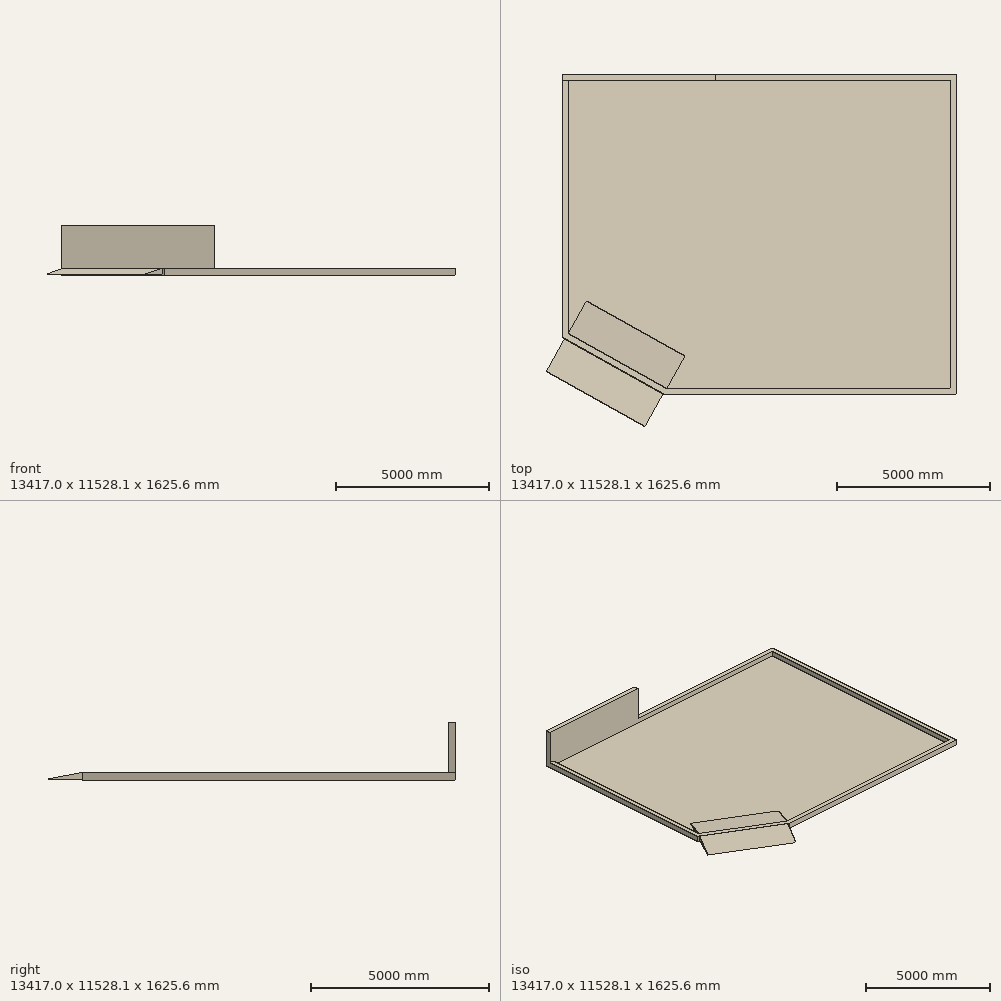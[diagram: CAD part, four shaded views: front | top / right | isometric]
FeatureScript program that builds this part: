
annotation { "Feature Type Name" : "Feature", "Feature Type Description" : "" }
export const myFeature = defineFeature(function(context is Context, id is Id, definition is map)
    precondition{}
    {
        {
            var Q0;
            Q0=qCreatedBy(makeId("Top.planeOp"),FACE);
            var sketch = newSketch(context, id + "F0", { "sketchPlane" : qUnion([Q0])});
            skLineSegment(sketch, "E0", {"start": v(-3030.3, -3459.43) * mm, "end": v(6240.7, -3459.43) * mm});
            skLineSegment(sketch, "E1", {"start": v(6240.7, -3459.43) * mm, "end": v(6240.7, 6624.37) * mm});
            skLineSegment(sketch, "E2", {"start": v(6240.7, 6624.37) * mm, "end": v(-6256.1, 6624.37) * mm});
            skLineSegment(sketch, "E3", {"start": v(-6256.1, 6624.37) * mm, "end": v(-6256.1, -1656.03) * mm});
            skLineSegment(sketch, "E4", {"start": v(-6256.1, -1656.03) * mm, "end": v(-3030.3, -3459.43) * mm});
            skLineSegment(sketch, "E5.0", {"start": v(6443.9, 6827.57) * mm, "end": v(-6459.3, 6827.57) * mm});
            skLineSegment(sketch, "E6.0", {"start": v(6443.9, -3662.63) * mm, "end": v(6443.9, 6827.57) * mm});
            skLineSegment(sketch, "E7.0", {"start": v(-3083.25, -3662.63) * mm, "end": v(6443.9, -3662.63) * mm});
            skLineSegment(sketch, "E8.0", {"start": v(-6459.3, 6827.57) * mm, "end": v(-6459.3, -1775.23) * mm});
            skLineSegment(sketch, "E9.0", {"start": v(-6459.3, -1775.23) * mm, "end": v(-3083.25, -3662.63) * mm});
            skLineSegment(sketch, "E10.filletArc", {"start": v(-6459.3, 6827.57) * mm, "end": v(-6459.3, 6827.57) * mm});
            skLineSegment(sketch, "E11.filletArc", {"start": v(6443.9, 6827.57) * mm, "end": v(6443.9, 6827.57) * mm});
            skLineSegment(sketch, "E12.filletArc", {"start": v(6443.9, -3662.63) * mm, "end": v(6443.9, -3662.63) * mm});
            skLineSegment(sketch, "E13.filletArc", {"start": v(-3083.25, -3662.63) * mm, "end": v(-3083.25, -3662.63) * mm});
            skLineSegment(sketch, "E14.filletArc", {"start": v(-6459.3, -1775.23) * mm, "end": v(-6459.3, -1775.23) * mm});
            skSolve(sketch);
        }
        {
            var Q0;
            Q0=makeQuery(id+"F0.imprint","IMPRINT",FACE,{"disambiguationData":[TD([[makeQuery(id+"F0.imprint","IMPRINT",EDGE,{"derivedFrom":sQuery(id+"F0.wireOp",EDGE,"E0")}),-1.0]])]});
            extrude(context, id + "F1", {"entities" : qUnion([Q0]), "depth" : 203.2 * mm, "offsetDistance" : 25.4 * mm});
        }
        {
            var Q0;
            Q0=makeQuery(id+"F1.opExtrude","CAP_FACE",FACE,{"disambiguationData":[OSD([sQuery(id+"F0.wireOp",EDGE,"E0"),sQuery(id+"F0.wireOp",EDGE,"E1"),sQuery(id+"F0.wireOp",EDGE,"E2"),sQuery(id+"F0.wireOp",EDGE,"E3"),sQuery(id+"F0.wireOp",EDGE,"E4"),sQuery(id+"F0.wireOp",EDGE,"E5.0"),sQuery(id+"F0.wireOp",EDGE,"E6.0"),sQuery(id+"F0.wireOp",EDGE,"E7.0"),sQuery(id+"F0.wireOp",EDGE,"E8.0"),sQuery(id+"F0.wireOp",EDGE,"E9.0")])],"isStart":false});
            var sketch = newSketch(context, id + "F2", { "sketchPlane" : qUnion([Q0])});
            skLineSegment(sketch, "E15.bottom", {"start": v(-6459.3, 6827.57) * mm, "end": v(-1430.1, 6827.57) * mm});
            skLineSegment(sketch, "E15.top", {"start": v(-6459.3, 6624.37) * mm, "end": v(-1430.1, 6624.37) * mm});
            skLineSegment(sketch, "E15.left", {"start": v(-6459.3, 6827.57) * mm, "end": v(-6459.3, 6624.37) * mm});
            skLineSegment(sketch, "E15.right", {"start": v(-1430.1, 6827.57) * mm, "end": v(-1430.1, 6624.37) * mm});
            skSolve(sketch);
        }
        {
            var Q0;
            Q0=makeQuery(id+"F2.imprint","IMPRINT",FACE,{"disambiguationData":[TD([[makeQuery(id+"F2.imprint","IMPRINT",EDGE,{"derivedFrom":sQuery(id+"F2.wireOp",EDGE,"E15.bottom")}),1.0]])]});
            extrude(context, id + "F3", {"entities" : qUnion([Q0]), "operationType" : NewBodyOperationType.ADD, "depth" : 1397 * mm, "offsetDistance" : 25.4 * mm});
        }
        {
            var Q0;
            Q0=qCreatedBy(makeId("Top.planeOp"),FACE);
            var sketch = newSketch(context, id + "F4", { "sketchPlane" : qUnion([Q0])});
            skLineSegment(sketch, "E16", {"start": v(-6256.1, -1656.03) * mm, "end": v(-3030.3, -3459.43) * mm});
            skLineSegment(sketch, "E17", {"start": v(-3030.3, -3459.43) * mm, "end": v(-2435.37, -2395.24) * mm});
            skLineSegment(sketch, "E18", {"start": v(-2435.37, -2395.24) * mm, "end": v(-5661.17, -591.84) * mm});
            skLineSegment(sketch, "E19", {"start": v(-5661.17, -591.84) * mm, "end": v(-6256.1, -1656.03) * mm});
            skLineSegment(sketch, "E20.MirrorCS", {"start": v(-3747.36, -4700.54) * mm, "end": v(-6973.16, -2897.14) * mm});
            skLineSegment(sketch, "E21.MirrorCS", {"start": v(-6973.16, -2897.14) * mm, "end": v(-6378.22, -1832.96) * mm});
            skLineSegment(sketch, "E22.MirrorCS", {"start": v(-6378.22, -1832.96) * mm, "end": v(-3152.42, -3636.36) * mm});
            skLineSegment(sketch, "E23.MirrorCS", {"start": v(-3152.42, -3636.36) * mm, "end": v(-3747.36, -4700.54) * mm});
            skSolve(sketch);
        }
        {
            var Q0;
            Q0=makeQuery(id+"F4.imprint","IMPRINT",FACE,{"disambiguationData":[TD([[makeQuery(id+"F4.imprint","IMPRINT",EDGE,{"derivedFrom":sQuery(id+"F4.wireOp",EDGE,"E20.MirrorCS")}),-1.0]])]});
            extrude(context, id + "F5", {"entities" : qUnion([Q0]), "depth" : 203.2 * mm, "offsetDistance" : 25.4 * mm});
        }
        {
            var Q0;
            Q0=makeQuery(id+"F4.imprint","IMPRINT",FACE,{"disambiguationData":[TD([[makeQuery(id+"F4.imprint","IMPRINT",EDGE,{"derivedFrom":sQuery(id+"F4.wireOp",EDGE,"E16")}),1.0]])]});
            extrude(context, id + "F6", {"entities" : qUnion([Q0]), "operationType" : NewBodyOperationType.ADD, "depth" : 203.2 * mm, "offsetDistance" : 25.4 * mm});
        }
        {
            var Q0;
            Q0=makeQuery(id+"F0.imprint","IMPRINT",FACE,{"disambiguationData":[TD([[makeQuery(id+"F0.imprint","IMPRINT",EDGE,{"derivedFrom":sQuery(id+"F0.wireOp",EDGE,"E0")}),-1.0]])]});
            var Q1;
            Q1=makeQuery(id+"F0.imprint","IMPRINT",FACE,{"disambiguationData":[TD([[makeQuery(id+"F0.imprint","IMPRINT",EDGE,{"derivedFrom":sQuery(id+"F0.wireOp",EDGE,"E0")}),1.0]])]});
            extrude(context, id + "F7", {"entities" : qUnion([Q0, Q1]), "operationType" : NewBodyOperationType.ADD, "oppositeDirection" : true, "depth" : 25.4 * mm, "offsetDistance" : 25.4 * mm});
        }
        {
            var Q0;
            Q0=makeQuery(id+"F5.opExtrude","SWEPT_FACE",FACE,{"disambiguationData":[OSD([sQuery(id+"F4.wireOp",EDGE,"E23.MirrorCS")])]});
            var sketch = newSketch(context, id + "F8", { "sketchPlane" : qUnion([Q0])});
            skLineSegment(sketch, "E24", {"start": v(-5931.52, 0) * mm, "end": v(-4712.32, 203.2) * mm});
            skLineSegment(sketch, "E25", {"start": v(-4712.32, 203.2) * mm, "end": v(-4712.32, 473.08) * mm});
            skLineSegment(sketch, "E26", {"start": v(-4712.32, 473.08) * mm, "end": v(-5931.52, 203.2) * mm});
            skLineSegment(sketch, "E27", {"start": v(-5931.52, 203.2) * mm, "end": v(-5931.52, 0) * mm});
            skLineSegment(sketch, "E28", {"start": v(-4712.32, 473.08) * mm, "end": v(-4712.32, 203.2) * mm});
            skSolve(sketch);
        }
        {
            var Q0;
            Q0=makeQuery(id+"F8.imprint","IMPRINT",FACE,{"disambiguationData":[TD([[makeQuery(id+"F8.imprint","IMPRINT",EDGE,{"derivedFrom":sQuery(id+"F8.wireOp",EDGE,"E24")}),1.0]])]});
            extrude(context, id + "F9", {"entities" : qUnion([Q0]), "operationType" : NewBodyOperationType.REMOVE, "oppositeDirection" : true, "depth" : 3784.6 * mm, "offsetDistance" : 25.4 * mm});
        }
        {
            var Q0;
            Q0=makeQuery(id+"F6.opExtrude","SWEPT_FACE",FACE,{"disambiguationData":[OSD([sQuery(id+"F4.wireOp",EDGE,"E17")])]});
            var sketch = newSketch(context, id + "F10", { "sketchPlane" : qUnion([Q0])});
            skLineSegment(sketch, "E29", {"start": v(-4498.3, 203.2) * mm, "end": v(-3279.1, 0) * mm});
            skLineSegment(sketch, "E30", {"start": v(-3279.1, 0) * mm, "end": v(-3279.1, 203.2) * mm});
            skLineSegment(sketch, "E31", {"start": v(-3279.1, 203.2) * mm, "end": v(-4498.3, 203.2) * mm});
            skSolve(sketch);
        }
        {
            var Q0;
            Q0=makeQuery(id+"F10.imprint","IMPRINT",FACE,{"disambiguationData":[TD([[makeQuery(id+"F10.imprint","IMPRINT",EDGE,{"derivedFrom":sQuery(id+"F10.wireOp",EDGE,"E29")}),1.0]])]});
            extrude(context, id + "F11", {"entities" : qUnion([Q0]), "operationType" : NewBodyOperationType.REMOVE, "oppositeDirection" : true, "depth" : 3708.4 * mm, "offsetDistance" : 25.4 * mm});
        }
    });
